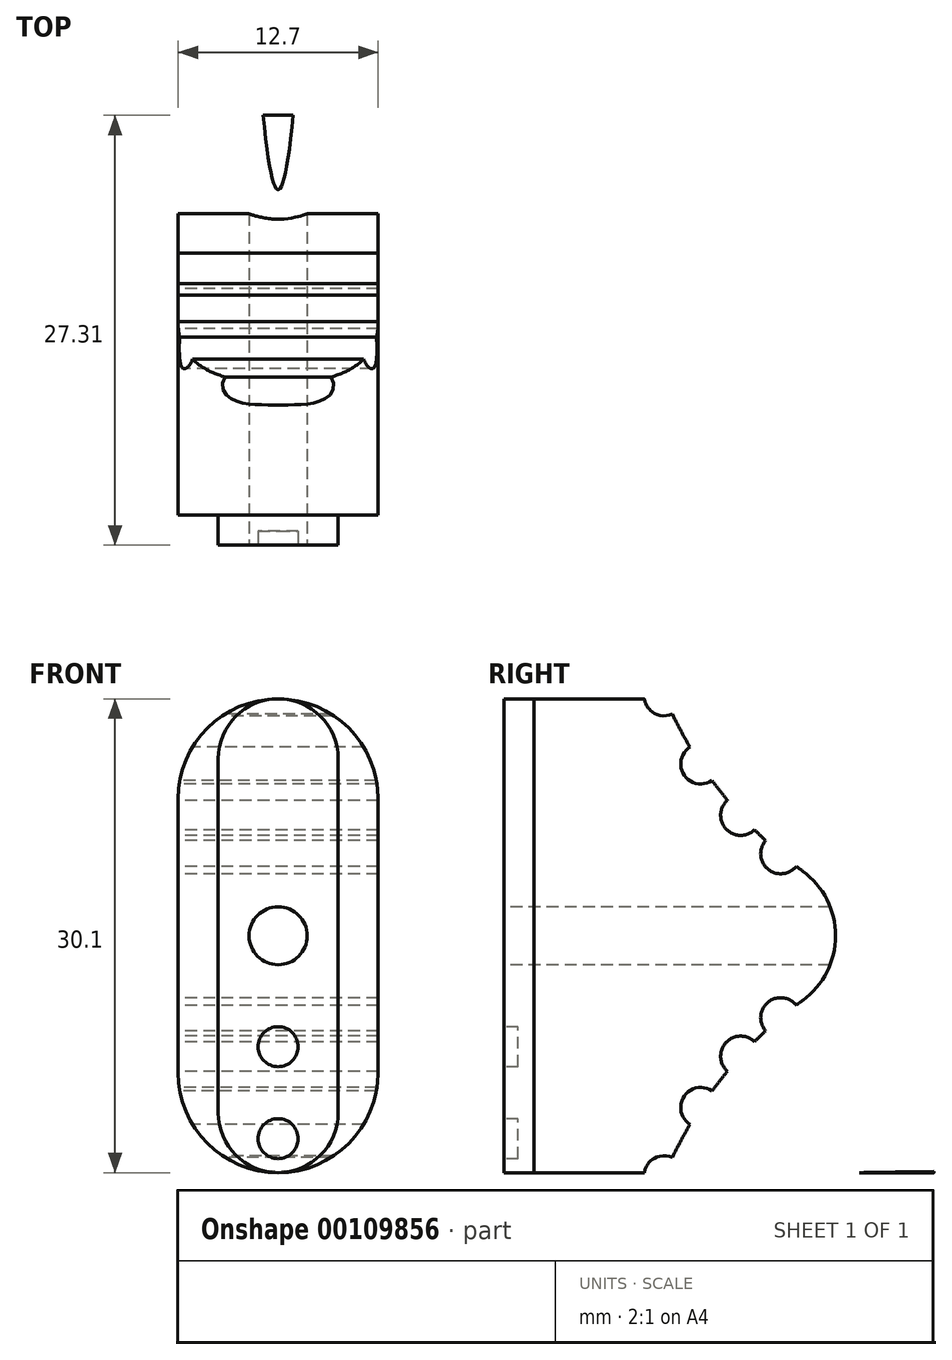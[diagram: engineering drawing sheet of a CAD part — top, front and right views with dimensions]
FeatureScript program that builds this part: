
annotation { "Feature Type Name" : "Feature", "Feature Type Description" : "" }
export const myFeature = defineFeature(function(context is Context, id is Id, definition is map)
    precondition{}
    {
        {
            var Q0;
            Q0=qCreatedBy(makeId("Front.planeOp"),FACE);
            var sketch = newSketch(context, id + "F0", { "sketchPlane" : qUnion([Q0])});
            skArc(sketch, "E0", {"start": v(-3.81, 0) * mm, "mid": v(0, -3.81) * mm, "end": v(3.81, 0) * mm});
            skArc(sketch, "E1", {"start": v(3.8, 22.48) * mm, "mid": v(0, 26.29) * mm, "end": v(-3.81, 22.48) * mm});
            skLineSegment(sketch, "E2", {"start": v(-3.81, 22.48) * mm, "end": v(-3.81, 0) * mm});
            skLineSegment(sketch, "E3", {"start": v(3.8, 22.48) * mm, "end": v(3.8, 0) * mm});
            skSolve(sketch);
        }
        {
            var Q0;
            Q0=makeQuery(id+"F0.imprint","IMPRINT",FACE,{"disambiguationData":[TD([[makeQuery(id+"F0.imprint","IMPRINT",EDGE,{"derivedFrom":sQuery(id+"F0.wireOp",EDGE,"E0")}),1.0]])]});
            extrude(context, id + "F1", {"entities" : qUnion([Q0]), "depth" : 1.9 * mm});
        }
        {
            var Q0;
            Q0=makeQuery(id+"F1.opExtrude","CAP_FACE",FACE,{"disambiguationData":[OSD([sQuery(id+"F0.wireOp",EDGE,"E0"),sQuery(id+"F0.wireOp",EDGE,"E1"),sQuery(id+"F0.wireOp",EDGE,"E2"),sQuery(id+"F0.wireOp",EDGE,"E3")])],"isStart":false});
            var sketch = newSketch(context, id + "F2", { "sketchPlane" : qUnion([Q0])});
            skLineSegment(sketch, "E4", {"start": v(0, 26.29) * mm, "end": v(0, -3.8) * mm, "construction": true});
            skLineSegment(sketch, "E5", {"start": v(-3.81, 11.24) * mm, "end": v(3.8, 11.24) * mm, "construction": true});
            skCircle(sketch, "E6", {"center": v(0, 11.24) * mm, "radius": 1.84 * mm});
            skCircle(sketch, "E7", {"center": v(0, 4.2) * mm, "radius": 1.27 * mm});
            skCircle(sketch, "E8", {"center": v(0, -1.65) * mm, "radius": 1.27 * mm});
            skSolve(sketch);
        }
        {
            var Q0;
            Q0=makeQuery(id+"F2.imprint","IMPRINT",FACE,{"disambiguationData":[TD([[makeQuery(id+"F2.imprint","IMPRINT",EDGE,{"derivedFrom":sQuery(id+"F2.wireOp",EDGE,"E7")}),1.0]])]});
            var Q1;
            Q1=makeQuery(id+"F2.imprint","IMPRINT",FACE,{"disambiguationData":[TD([[makeQuery(id+"F2.imprint","IMPRINT",EDGE,{"derivedFrom":sQuery(id+"F2.wireOp",EDGE,"E8")}),1.0]])]});
            extrude(context, id + "F3", {"entities" : qUnion([Q0, Q1]), "operationType" : NewBodyOperationType.REMOVE, "oppositeDirection" : true, "depth" : 0.89 * mm});
        }
        {
            var Q0;
            Q0=makeQuery(id+"F2.imprint","IMPRINT",FACE,{"disambiguationData":[TD([[makeQuery(id+"F2.imprint","IMPRINT",EDGE,{"derivedFrom":sQuery(id+"F2.wireOp",EDGE,"E6")}),1.0]])]});
            extrude(context, id + "F4", {"entities" : qUnion([Q0]), "operationType" : NewBodyOperationType.REMOVE, "oppositeDirection" : true, "depth" : 25.4 * mm});
        }
        {
            var Q0;
            Q0=makeQuery(id+"F1.opExtrude","CAP_FACE",FACE,{"disambiguationData":[OSD([sQuery(id+"F0.wireOp",EDGE,"E0"),sQuery(id+"F0.wireOp",EDGE,"E1"),sQuery(id+"F0.wireOp",EDGE,"E2"),sQuery(id+"F0.wireOp",EDGE,"E3")])],"isStart":true});
            var sketch = newSketch(context, id + "F5", { "sketchPlane" : qUnion([Q0])});
            skLineSegment(sketch, "E9", {"start": v(0, 26.29) * mm, "end": v(0, -3.8) * mm, "construction": true});
            skArc(sketch, "E10", {"start": v(6.35, 19.94) * mm, "mid": v(0, 26.29) * mm, "end": v(-6.35, 19.94) * mm});
            skArc(sketch, "E11", {"start": v(-6.35, 2.54) * mm, "mid": v(0, -3.81) * mm, "end": v(6.35, 2.54) * mm});
            skLineSegment(sketch, "E12", {"start": v(-6.35, 19.94) * mm, "end": v(-6.35, 2.54) * mm});
            skLineSegment(sketch, "E13", {"start": v(6.35, 19.94) * mm, "end": v(6.35, 2.54) * mm});
            skSolve(sketch);
        }
        {
            var Q0;
            {var subQ1=sQuery(id+"F5.wireOp",EDGE,"E13");Q0=makeQuery(id+"F5.imprint","IMPRINT",FACE,{"disambiguationData":[TD([[makeQuery(id+"F5.imprint","IMPRINT",EDGE,{"derivedFrom":subQ1}),-1.0]])]});}
            var Q1;
            {var subQ0=sQuery(id+"F0.wireOp",EDGE,"E2");var subQ1=makeQuery(id+"F1.opExtrude","CAP_EDGE",EDGE,{"disambiguationData":[OSD([subQ0])],"isStart":true});Q1=makeQuery(id+"F5.imprint","IMPRINT",FACE,{"disambiguationData":[TD([[makeQuery(id+"F5.imprint","IMPRINT",EDGE,{"derivedFrom":subQ1}),-1.0]])]});}
            var Q2;
            {var subQ1=sQuery(id+"F5.wireOp",EDGE,"E12");Q2=makeQuery(id+"F5.imprint","IMPRINT",FACE,{"disambiguationData":[TD([[makeQuery(id+"F5.imprint","IMPRINT",EDGE,{"derivedFrom":subQ1}),1.0]])]});}
            extrude(context, id + "F6", {"entities" : qUnion([Q0, Q1, Q2]), "operationType" : NewBodyOperationType.ADD, "depth" : 25.4 * mm});
        }
        {
            var Q0;
            Q0=makeQuery(id+"F6.opExtrude","SWEPT_FACE",FACE,{"disambiguationData":[OSD([sQuery(id+"F5.wireOp",EDGE,"E13")])]});
            var sketch = newSketch(context, id + "F7", { "sketchPlane" : qUnion([Q0])});
            skLineSegment(sketch, "E14", {"start": v(-25.4, 11.24) * mm, "end": v(0, 11.24) * mm, "construction": true});
            skArc(sketch, "E15", {"start": v(-17.07, 15.34) * mm, "mid": v(-16.86, 15.5) * mm, "end": v(-16.65, 15.65) * mm});
            skPoint(sketch, "E15.second.point", {"position": v(-8.26, 26.48) * mm});
            skPoint(sketch, "E15.third.point", {"position": v(-51.71, 55.68) * mm});
            skArc(sketch, "E16", {"start": v(-8.78, -2.84) * mm, "mid": v(-9.32, -1.78) * mm, "end": v(-9.9, -0.74) * mm});
            skPoint(sketch, "E16.second.point", {"position": v(-8.26, -4) * mm});
            skPoint(sketch, "E16.third.point", {"position": v(-56.6, -26.47) * mm});
            skArc(sketch, "E17", {"start": v(-17.07, 15.34) * mm, "mid": v(-19.15, 11.24) * mm, "end": v(-17.07, 7.14) * mm});
            skLineSegment(sketch, "E18", {"start": v(-8.25, 26.48) * mm, "end": v(-8.26, -4) * mm, "construction": true});
            skLineSegment(sketch, "E19", {"start": v(-10.58, 22.15) * mm, "end": v(-10.58, 0.33) * mm, "construction": true});
            skLineSegment(sketch, "E20", {"start": v(-13.12, 3.6) * mm, "end": v(-13.12, 18.89) * mm, "construction": true});
            skLineSegment(sketch, "E21", {"start": v(-15.66, 16.45) * mm, "end": v(-15.66, 6.03) * mm, "construction": true});
            skArc(sketch, "E22", {"start": v(-8.78, 25.32) * mm, "mid": v(-7.18, 27.16) * mm, "end": v(-9.52, 26.5) * mm});
            skArc(sketch, "E23", {"start": v(-11.3, 21.1) * mm, "mid": v(-9.52, 21.45) * mm, "end": v(-9.9, 23.22) * mm});
            skArc(sketch, "E24", {"start": v(-14, 17.97) * mm, "mid": v(-12.18, 18.03) * mm, "end": v(-12.28, 19.84) * mm});
            skArc(sketch, "E25", {"start": v(-16.65, 15.65) * mm, "mid": v(-14.84, 15.47) * mm, "end": v(-14.7, 17.29) * mm});
            skArc(sketch, "E26", {"start": v(-9.52, -3.98) * mm, "mid": v(-7.2, -4.7) * mm, "end": v(-8.78, -2.84) * mm});
            skArc(sketch, "E27", {"start": v(-9.9, -0.74) * mm, "mid": v(-9.52, 1.03) * mm, "end": v(-11.3, 1.38) * mm});
            skArc(sketch, "E28", {"start": v(-12.28, 2.63) * mm, "mid": v(-12.18, 4.45) * mm, "end": v(-14, 4.51) * mm});
            skArc(sketch, "E29", {"start": v(-14.7, 5.2) * mm, "mid": v(-14.84, 7) * mm, "end": v(-16.65, 6.83) * mm});
            skArc(sketch, "E30.trimOffspring", {"start": v(-14.7, 17.29) * mm, "mid": v(-14.35, 17.62) * mm, "end": v(-14, 17.97) * mm});
            skArc(sketch, "E31.trimOffspring", {"start": v(-12.28, 19.84) * mm, "mid": v(-11.78, 20.47) * mm, "end": v(-11.3, 21.1) * mm});
            skArc(sketch, "E32.trimOffspring", {"start": v(-11.3, 1.38) * mm, "mid": v(-11.78, 2.01) * mm, "end": v(-12.28, 2.63) * mm});
            skArc(sketch, "E33.trimOffspring", {"start": v(-14, 4.51) * mm, "mid": v(-14.35, 4.86) * mm, "end": v(-14.7, 5.2) * mm});
            skArc(sketch, "E34.trimOffspring", {"start": v(-16.65, 6.83) * mm, "mid": v(-16.86, 6.99) * mm, "end": v(-17.07, 7.14) * mm});
            skArc(sketch, "E35.trimOffspring", {"start": v(-9.9, 23.22) * mm, "mid": v(-9.32, 24.26) * mm, "end": v(-8.78, 25.32) * mm});
            skLineSegment(sketch, "E36", {"start": v(-25.4, 19.94) * mm, "end": v(-25.4, 26.84) * mm});
            skLineSegment(sketch, "E37", {"start": v(-25.4, 26.84) * mm, "end": v(-9.52, 26.5) * mm});
            skLineSegment(sketch, "E38", {"start": v(-25.4, 2.54) * mm, "end": v(-25.4, -3.74) * mm});
            skLineSegment(sketch, "E39", {"start": v(-25.4, -3.74) * mm, "end": v(-9.52, -3.98) * mm});
            skSolve(sketch);
        }
        {
            var Q0;
            Q0=makeQuery(id+"F7.imprint","IMPRINT",FACE,{"disambiguationData":[TD([[makeQuery(id+"F7.imprint","IMPRINT",EDGE,{"derivedFrom":sQuery(id+"F7.wireOp",EDGE,"E22")}),1.0]])]});
            var Q1;
            Q1=makeQuery(id+"F7.imprint","IMPRINT",FACE,{"disambiguationData":[TD([[makeQuery(id+"F7.imprint","IMPRINT",EDGE,{"derivedFrom":sQuery(id+"F7.wireOp",EDGE,"E15")}),1.0]])]});
            var Q2;
            Q2=makeQuery(id+"F7.imprint","IMPRINT",FACE,{"disambiguationData":[TD([[makeQuery(id+"F7.imprint","IMPRINT",EDGE,{"derivedFrom":sQuery(id+"F7.wireOp",EDGE,"E16")}),1.0]])]});
            extrude(context, id + "F8", {"entities" : qUnion([Q0, Q1, Q2]), "operationType" : NewBodyOperationType.REMOVE, "oppositeDirection" : true, "depth" : 25.4 * mm});
        }
    });
